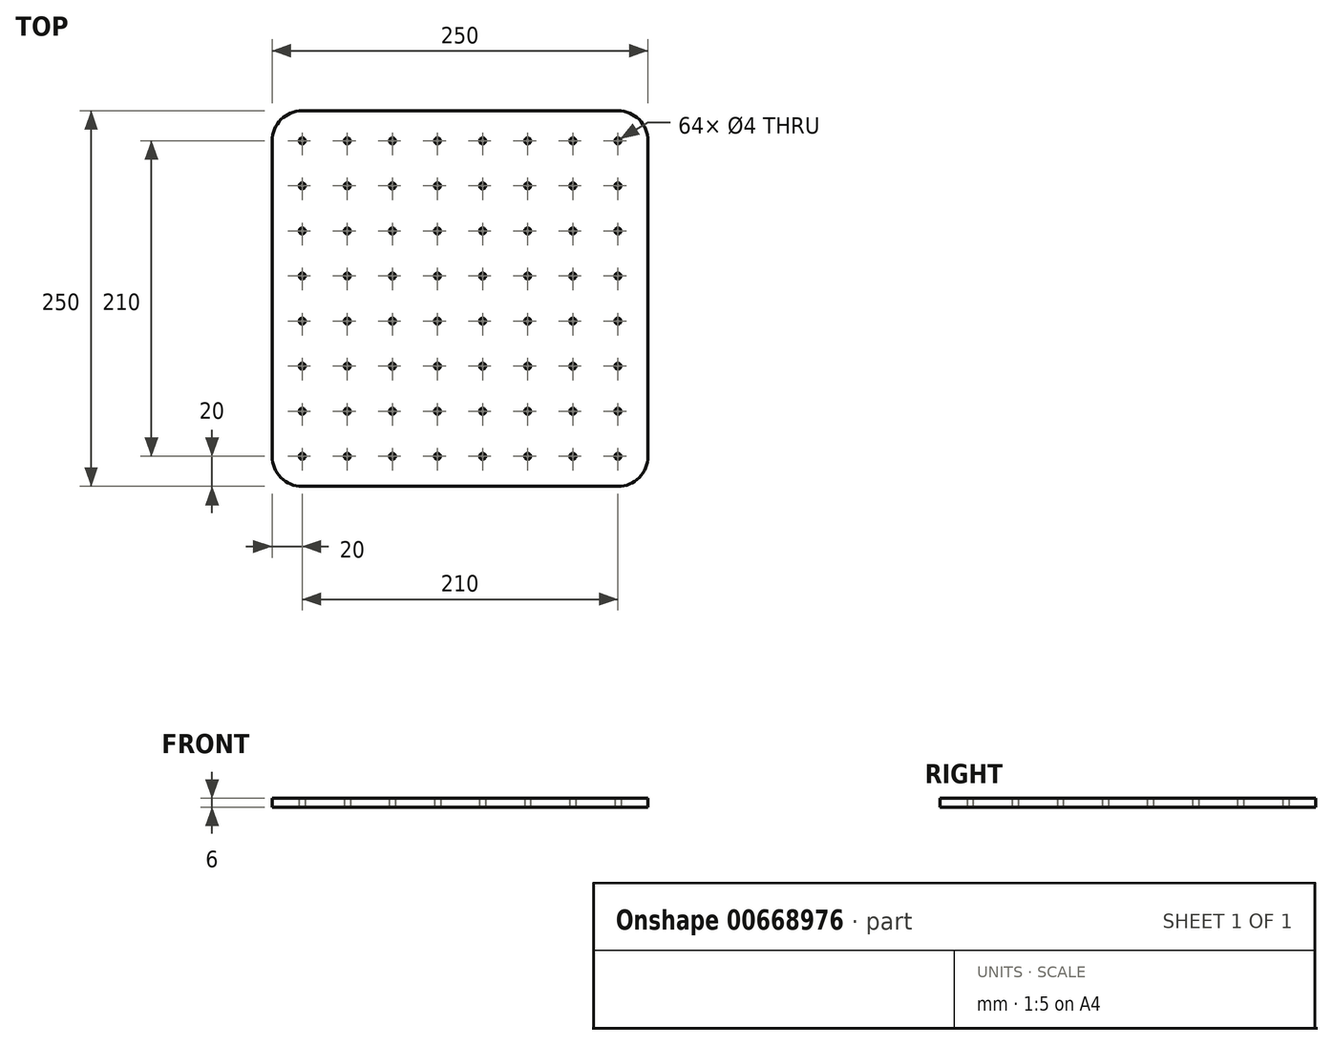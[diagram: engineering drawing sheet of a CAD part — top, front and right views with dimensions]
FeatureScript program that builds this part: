
annotation { "Feature Type Name" : "Feature", "Feature Type Description" : "" }
export const myFeature = defineFeature(function(context is Context, id is Id, definition is map)
    precondition{}
    {
        {
            var Q0;
            Q0=qCreatedBy(makeId("Top.planeOp"),FACE);
            var sketch = newSketch(context, id + "F0", { "sketchPlane" : qUnion([Q0])});
            skLineSegment(sketch, "E0.bottom", {"start": v(-105, 125) * mm, "end": v(105, 125) * mm});
            skLineSegment(sketch, "E0.top", {"start": v(-105, -125) * mm, "end": v(105, -125) * mm});
            skLineSegment(sketch, "E0.left", {"start": v(-125, 105) * mm, "end": v(-125, -105) * mm});
            skLineSegment(sketch, "E0.right", {"start": v(125, 105) * mm, "end": v(125, -105) * mm});
            skPoint(sketch, "E0.middle", {"position": v(0, 0) * mm});
            skPoint(sketch, "E1.visualSharp", {"position": v(-125, 125) * mm});
            skArc(sketch, "E1.filletArc", {"start": v(-105, 125) * mm, "mid": v(-119.14, 119.14) * mm, "end": v(-125, 105) * mm});
            skPoint(sketch, "E2.visualSharp", {"position": v(125, 125) * mm});
            skArc(sketch, "E2.filletArc", {"start": v(125, 105) * mm, "mid": v(119.14, 119.14) * mm, "end": v(105, 125) * mm});
            skPoint(sketch, "E3.visualSharp", {"position": v(-125, -125) * mm});
            skArc(sketch, "E3.filletArc", {"start": v(-125, -105) * mm, "mid": v(-119.14, -119.14) * mm, "end": v(-105, -125) * mm});
            skPoint(sketch, "E4.visualSharp", {"position": v(125, -125) * mm});
            skArc(sketch, "E4.filletArc", {"start": v(105, -125) * mm, "mid": v(119.14, -119.14) * mm, "end": v(125, -105) * mm});
            skCircle(sketch, "E5", {"center": v(-105, 105) * mm, "radius": 2 * mm});
            skCircle(sketch, "E6.5.0.0", {"center": v(45, 105) * mm, "radius": 2 * mm});
            skCircle(sketch, "E7.0.1.0", {"center": v(-105, 75) * mm, "radius": 2 * mm});
            skCircle(sketch, "E7.0.2.0", {"center": v(-105, 45) * mm, "radius": 2 * mm});
            skCircle(sketch, "E7.0.3.0", {"center": v(-105, 15) * mm, "radius": 2 * mm});
            skCircle(sketch, "E7.0.4.0", {"center": v(-105, -15) * mm, "radius": 2 * mm});
            skCircle(sketch, "E7.0.5.0", {"center": v(-105, -45) * mm, "radius": 2 * mm});
            skCircle(sketch, "E7.0.6.0", {"center": v(-105, -75) * mm, "radius": 2 * mm});
            skCircle(sketch, "E7.0.7.0", {"center": v(-105, -105) * mm, "radius": 2 * mm});
            skCircle(sketch, "E7.1.0.0", {"center": v(-75, 105) * mm, "radius": 2 * mm});
            skCircle(sketch, "E7.1.1.0", {"center": v(-75, 75) * mm, "radius": 2 * mm});
            skCircle(sketch, "E7.1.2.0", {"center": v(-75, 45) * mm, "radius": 2 * mm});
            skCircle(sketch, "E7.1.3.0", {"center": v(-75, 15) * mm, "radius": 2 * mm});
            skCircle(sketch, "E7.1.4.0", {"center": v(-75, -15) * mm, "radius": 2 * mm});
            skCircle(sketch, "E7.1.5.0", {"center": v(-75, -45) * mm, "radius": 2 * mm});
            skCircle(sketch, "E7.1.6.0", {"center": v(-75, -75) * mm, "radius": 2 * mm});
            skCircle(sketch, "E7.1.7.0", {"center": v(-75, -105) * mm, "radius": 2 * mm});
            skCircle(sketch, "E7.2.0.0", {"center": v(-45, 105) * mm, "radius": 2 * mm});
            skCircle(sketch, "E7.2.1.0", {"center": v(-45, 75) * mm, "radius": 2 * mm});
            skCircle(sketch, "E7.2.2.0", {"center": v(-45, 45) * mm, "radius": 2 * mm});
            skCircle(sketch, "E7.2.3.0", {"center": v(-45, 15) * mm, "radius": 2 * mm});
            skCircle(sketch, "E7.2.4.0", {"center": v(-45, -15) * mm, "radius": 2 * mm});
            skCircle(sketch, "E7.2.5.0", {"center": v(-45, -45) * mm, "radius": 2 * mm});
            skCircle(sketch, "E7.2.6.0", {"center": v(-45, -75) * mm, "radius": 2 * mm});
            skCircle(sketch, "E7.2.7.0", {"center": v(-45, -105) * mm, "radius": 2 * mm});
            skCircle(sketch, "E7.3.0.0", {"center": v(-15, 105) * mm, "radius": 2 * mm});
            skCircle(sketch, "E7.3.1.0", {"center": v(-15, 75) * mm, "radius": 2 * mm});
            skCircle(sketch, "E7.3.2.0", {"center": v(-15, 45) * mm, "radius": 2 * mm});
            skCircle(sketch, "E7.3.3.0", {"center": v(-15, 15) * mm, "radius": 2 * mm});
            skCircle(sketch, "E7.3.4.0", {"center": v(-15, -15) * mm, "radius": 2 * mm});
            skCircle(sketch, "E7.3.5.0", {"center": v(-15, -45) * mm, "radius": 2 * mm});
            skCircle(sketch, "E7.3.6.0", {"center": v(-15, -75) * mm, "radius": 2 * mm});
            skCircle(sketch, "E7.3.7.0", {"center": v(-15, -105) * mm, "radius": 2 * mm});
            skCircle(sketch, "E7.4.0.0", {"center": v(15, 105) * mm, "radius": 2 * mm});
            skCircle(sketch, "E7.4.1.0", {"center": v(15, 75) * mm, "radius": 2 * mm});
            skCircle(sketch, "E7.4.2.0", {"center": v(15, 45) * mm, "radius": 2 * mm});
            skCircle(sketch, "E7.4.3.0", {"center": v(15, 15) * mm, "radius": 2 * mm});
            skCircle(sketch, "E7.4.4.0", {"center": v(15, -15) * mm, "radius": 2 * mm});
            skCircle(sketch, "E7.4.5.0", {"center": v(15, -45) * mm, "radius": 2 * mm});
            skCircle(sketch, "E7.4.6.0", {"center": v(15, -75) * mm, "radius": 2 * mm});
            skCircle(sketch, "E7.4.7.0", {"center": v(15, -105) * mm, "radius": 2 * mm});
            skCircle(sketch, "E7.5.1.0", {"center": v(45, 75) * mm, "radius": 2 * mm});
            skCircle(sketch, "E7.5.2.0", {"center": v(45, 45) * mm, "radius": 2 * mm});
            skCircle(sketch, "E7.5.3.0", {"center": v(45, 15) * mm, "radius": 2 * mm});
            skCircle(sketch, "E7.5.4.0", {"center": v(45, -15) * mm, "radius": 2 * mm});
            skCircle(sketch, "E7.5.5.0", {"center": v(45, -45) * mm, "radius": 2 * mm});
            skCircle(sketch, "E7.5.6.0", {"center": v(45, -75) * mm, "radius": 2 * mm});
            skCircle(sketch, "E7.5.7.0", {"center": v(45, -105) * mm, "radius": 2 * mm});
            skCircle(sketch, "E7.6.0.0", {"center": v(75, 105) * mm, "radius": 2 * mm});
            skCircle(sketch, "E7.6.1.0", {"center": v(75, 75) * mm, "radius": 2 * mm});
            skCircle(sketch, "E7.6.2.0", {"center": v(75, 45) * mm, "radius": 2 * mm});
            skCircle(sketch, "E7.6.3.0", {"center": v(75, 15) * mm, "radius": 2 * mm});
            skCircle(sketch, "E7.6.4.0", {"center": v(75, -15) * mm, "radius": 2 * mm});
            skCircle(sketch, "E7.6.5.0", {"center": v(75, -45) * mm, "radius": 2 * mm});
            skCircle(sketch, "E7.6.6.0", {"center": v(75, -75) * mm, "radius": 2 * mm});
            skCircle(sketch, "E7.6.7.0", {"center": v(75, -105) * mm, "radius": 2 * mm});
            skCircle(sketch, "E7.7.0.0", {"center": v(105, 105) * mm, "radius": 2 * mm});
            skCircle(sketch, "E7.7.1.0", {"center": v(105, 75) * mm, "radius": 2 * mm});
            skCircle(sketch, "E7.7.2.0", {"center": v(105, 45) * mm, "radius": 2 * mm});
            skCircle(sketch, "E7.7.3.0", {"center": v(105, 15) * mm, "radius": 2 * mm});
            skCircle(sketch, "E7.7.4.0", {"center": v(105, -15) * mm, "radius": 2 * mm});
            skCircle(sketch, "E7.7.5.0", {"center": v(105, -45) * mm, "radius": 2 * mm});
            skCircle(sketch, "E7.7.6.0", {"center": v(105, -75) * mm, "radius": 2 * mm});
            skCircle(sketch, "E7.7.7.0", {"center": v(105, -105) * mm, "radius": 2 * mm});
            skLineSegment(sketch, "E7.direction1", {"start": v(-105, 105) * mm, "end": v(-75, 105) * mm, "construction": true});
            skLineSegment(sketch, "E7.direction2", {"start": v(-105, 105) * mm, "end": v(-105, 75) * mm, "construction": true});
            skSolve(sketch);
        }
        {
            var Q0;
            Q0 = qSketchRegion(id + "F0", true);
            extrude(context, id + "F1", {"entities" : qUnion([Q0]), "depth" : 6 * mm, "offsetDistance" : 25 * mm});
        }
    });
